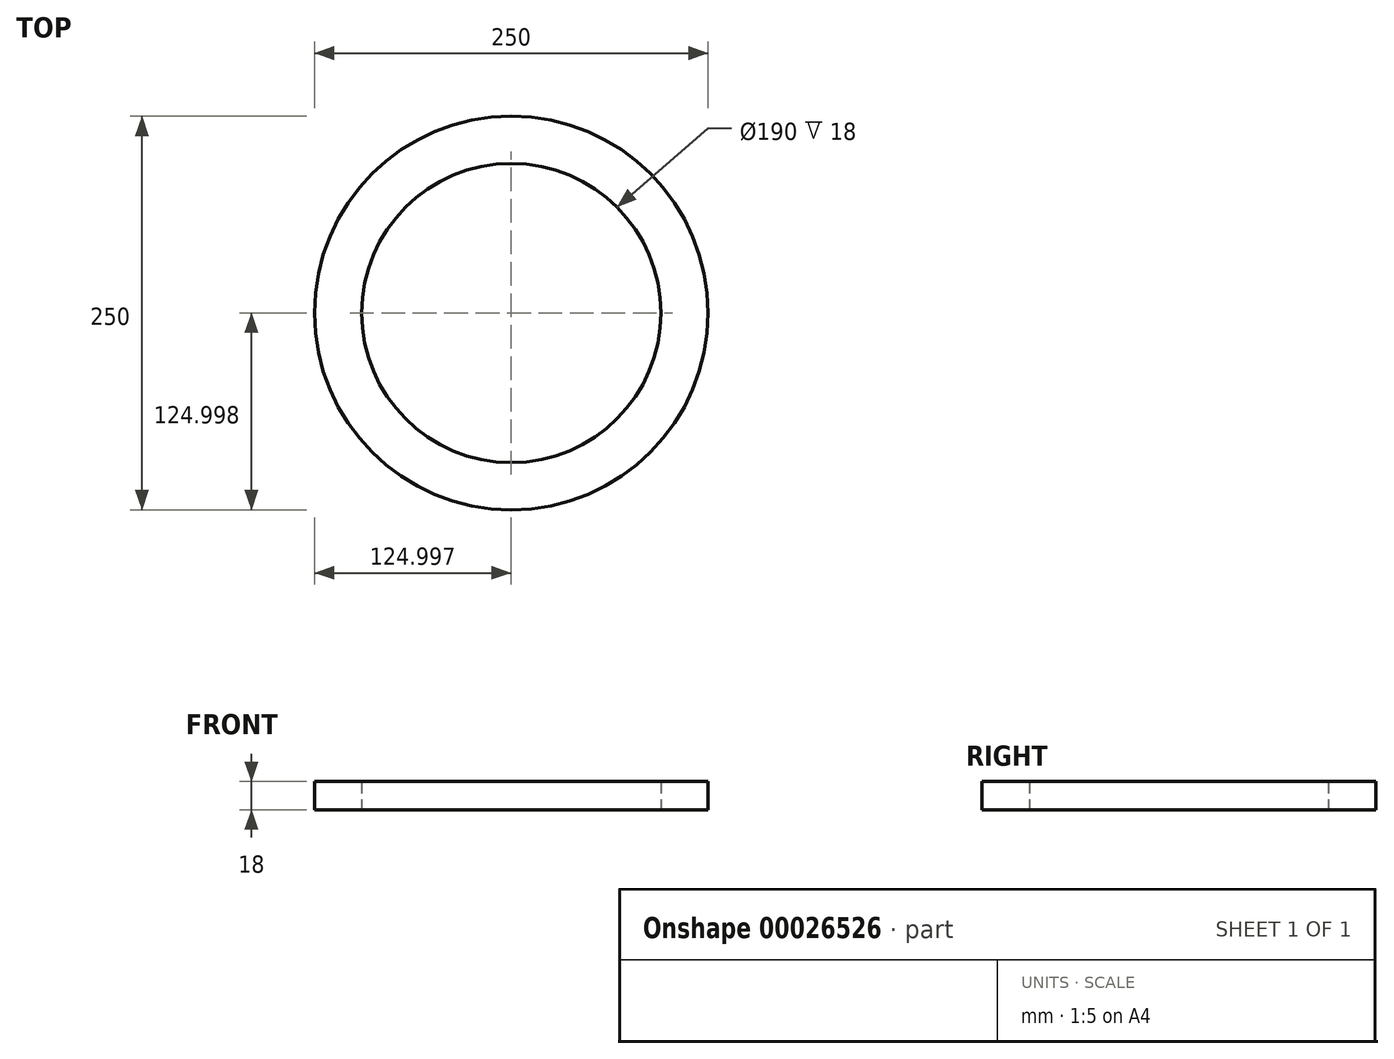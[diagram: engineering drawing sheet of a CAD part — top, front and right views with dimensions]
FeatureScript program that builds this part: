
annotation { "Feature Type Name" : "Feature", "Feature Type Description" : "" }
export const myFeature = defineFeature(function(context is Context, id is Id, definition is map)
    precondition{}
    {
        {
            var Q0;
            Q0=qCreatedBy(makeId("Top.planeOp"),FACE);
            var sketch = newSketch(context, id + "F0", { "sketchPlane" : qUnion([Q0])});
            skCircle(sketch, "E0", {"center": v(-45.07, -27.68) * mm, "radius": 125 * mm});
            skCircle(sketch, "E1", {"center": v(-45.07, -27.68) * mm, "radius": 95 * mm});
            skSolve(sketch);
        }
        {
            var Q0;
            Q0 = qSketchRegion(id + "F0", true);
            extrude(context, id + "F1", {"entities" : qUnion([Q0]), "depth" : 18 * mm});
        }
    });
